# Revit family: Domotics-DomesticRanges-GEWISS-CHORUS_DATA-SOCKET-OUTLET_RJ11_2M
name_source: partatom
category: Apparecchi elettrici
revit_build: Autodesk Revit 2016 (Build: 20161004_0715(x64)
units: mm (PartAtom-declared; Revit-internal decimal feet)

## family parameters
Condiviso = Sì
Host = Superficie
Mantenere orientamento annotazione = Sì
Numero OmniClass = 23.80.50.14
Punto di calcolo locali = Sì
Quota connettore circolare = Usa diametro
Taglio con vuoti quando caricato = Sì
Tipo di parte = Normale
Titolo OmniClass = Plug Connectors

## types (3) — shared parameters
Carico apparente = 0 VA
Catalogue = DOMOTICS
Catalogue Range = CHORUS - DOMESTIC RANGE
Electrocod = 0131
IDF = bd7f6670-6fad-444b-86b0-eef888e40e5d
IDT = 580700dd-a6fb-4dbd-ab20-41a3a807ffa7
Immagine tipo = GW14409.jpg
Larghezza presa = 46 mm  [stored 0.150919 ft]
N. poli = 1
Offset bidimensionale7 = 2 mm  [stored 0.00656168 ft]
Produttore = GEWISS S.p.A.
Prospetto di default = 1219 mm
Simbolo = SIMBOLO PRESE TELEFONO : PRESA TEL
Technical sheet = https://www.gewiss.com
Tipo = CHORUS PRESE RJ11_BASE : TITANIO
URL = https://www.gewiss.com
Version file RFA = 19.0
Volt = 230 V

## per-type parameters (varying)
| type | Descrizione | EAN code | Modello |
| GW10409 - TELEPHONE CONNECTOR RJ11 2M WHITE | TELEPHONE CONNECTOR RJ11 2M WHITE | 8011564823761 | GW10409 |
| GW14409 - TELEPHONE CONNECTOR RJ11 2M TITANIUM | TELEPHONE CONNECTOR RJ11 2M TITANIUM | 8011564823785 | GW14409 |
| GW12409 - TELEPHONE CONNECTOR RJ11 2M BLACK | TELEPHONE CONNECTOR RJ11 2M BLACK | 8011564823778 | GW12409 |

note: [stored X ft] marks values corroborated as IEEE doubles in the binary element streams (Revit-internal decimal feet)

## geometry (parser evidence)
native form markers: Sweep x1
no freeform markers — native parametric forms only
